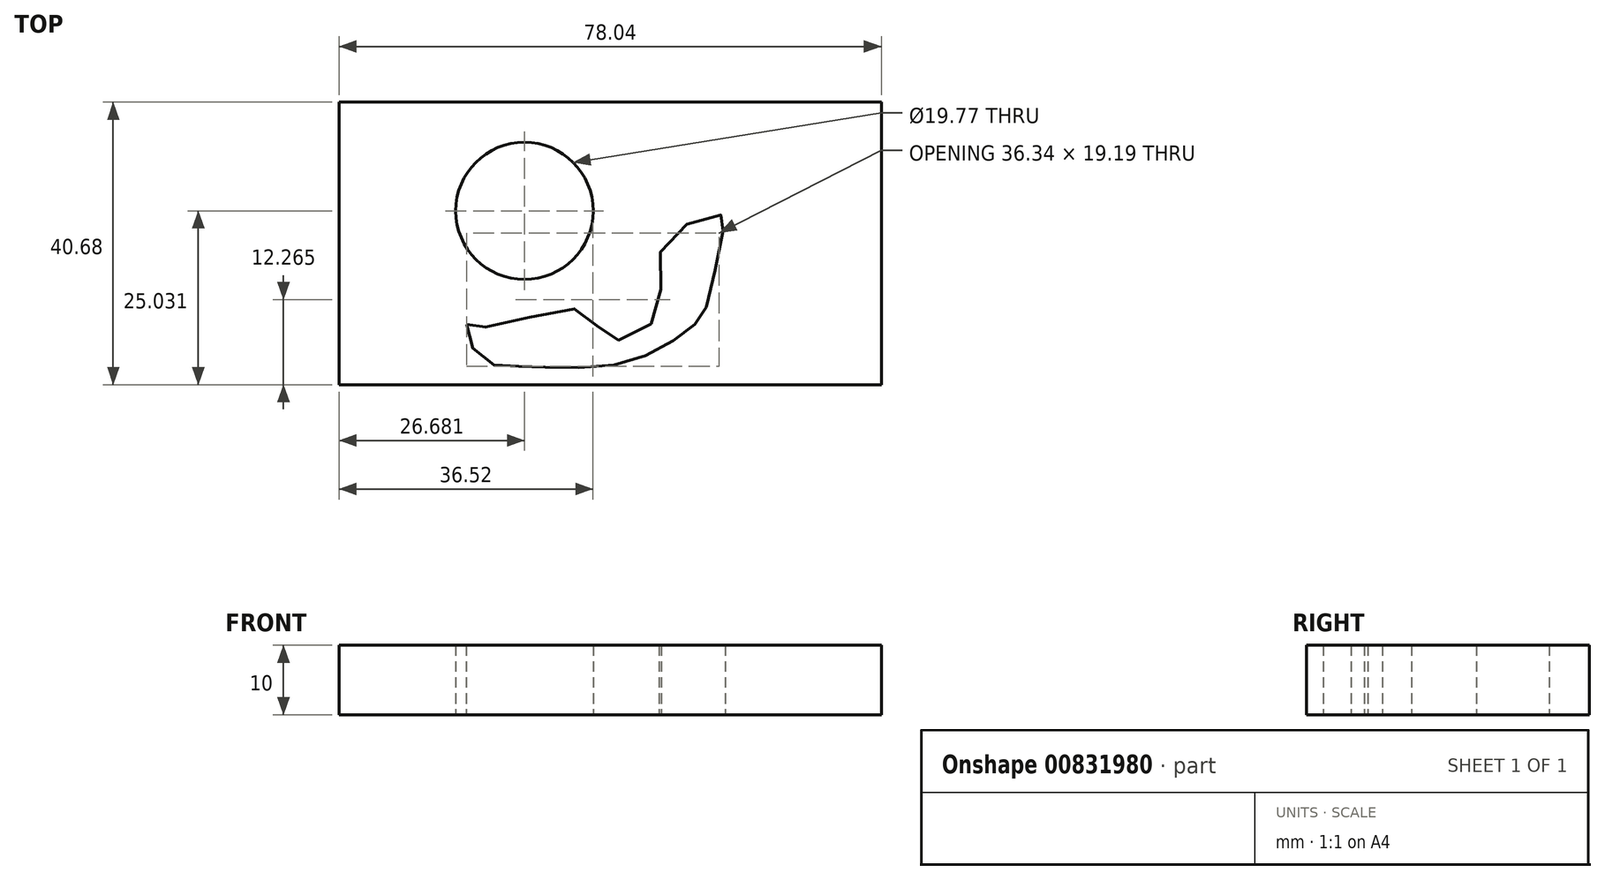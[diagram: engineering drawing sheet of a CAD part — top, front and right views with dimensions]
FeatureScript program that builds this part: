
annotation { "Feature Type Name" : "Feature", "Feature Type Description" : "" }
export const myFeature = defineFeature(function(context is Context, id is Id, definition is map)
    precondition{}
    {
        {
            var Q0;
            Q0=qCreatedBy(makeId("Top.planeOp"),FACE);
            var sketch = newSketch(context, id + "F0", { "sketchPlane" : qUnion([Q0])});
            skLineSegment(sketch, "E0.bottom", {"start": v(-57.53, -59.91) * mm, "end": v(20.51, -59.91) * mm});
            skLineSegment(sketch, "E0.top", {"start": v(-57.53, -19.23) * mm, "end": v(20.51, -19.23) * mm});
            skLineSegment(sketch, "E0.left", {"start": v(-57.53, -59.91) * mm, "end": v(-57.53, -19.23) * mm});
            skLineSegment(sketch, "E0.right", {"start": v(20.51, -59.91) * mm, "end": v(20.51, -19.23) * mm});
            skCircle(sketch, "E1", {"center": v(-30.85, -34.88) * mm, "radius": 9.88 * mm});
            skFitSpline(sketch, "E2", {"points": [v(-39.18, -51.23) * mm, v(-36.63, -51.61) * mm, v(-22.57, -49.18) * mm, v(-18.74, -53.27) * mm, v(-11.59, -49.57) * mm, v(-10.82, -39.6) * mm, v(-2.39, -35.51) * mm, v(-2.26, -37.56) * mm, v(-4.69, -48.67) * mm, v(-6.47, -51.35) * mm, v(-11.59, -54.8) * mm, v(-19.12, -57.23) * mm, v(-27.94, -57.36) * mm, v(-32.92, -57.23) * mm, v(-37.4, -55.95) * mm, v(-39.18, -51.23) * mm]});
            skSolve(sketch);
        }
        {
            var Q0;
            Q0=makeQuery(id+"F0.imprint","IMPRINT",FACE,{"disambiguationData":[TD([[makeQuery(id+"F0.imprint","IMPRINT",EDGE,{"derivedFrom":sQuery(id+"F0.wireOp",EDGE,"E0.bottom")}),1.0]])]});
            extrude(context, id + "F1", {"entities" : qUnion([Q0]), "depth" : 8 * mm + 2 * mm, "offsetDistance" : 25.4 * mm});
        }
    });
